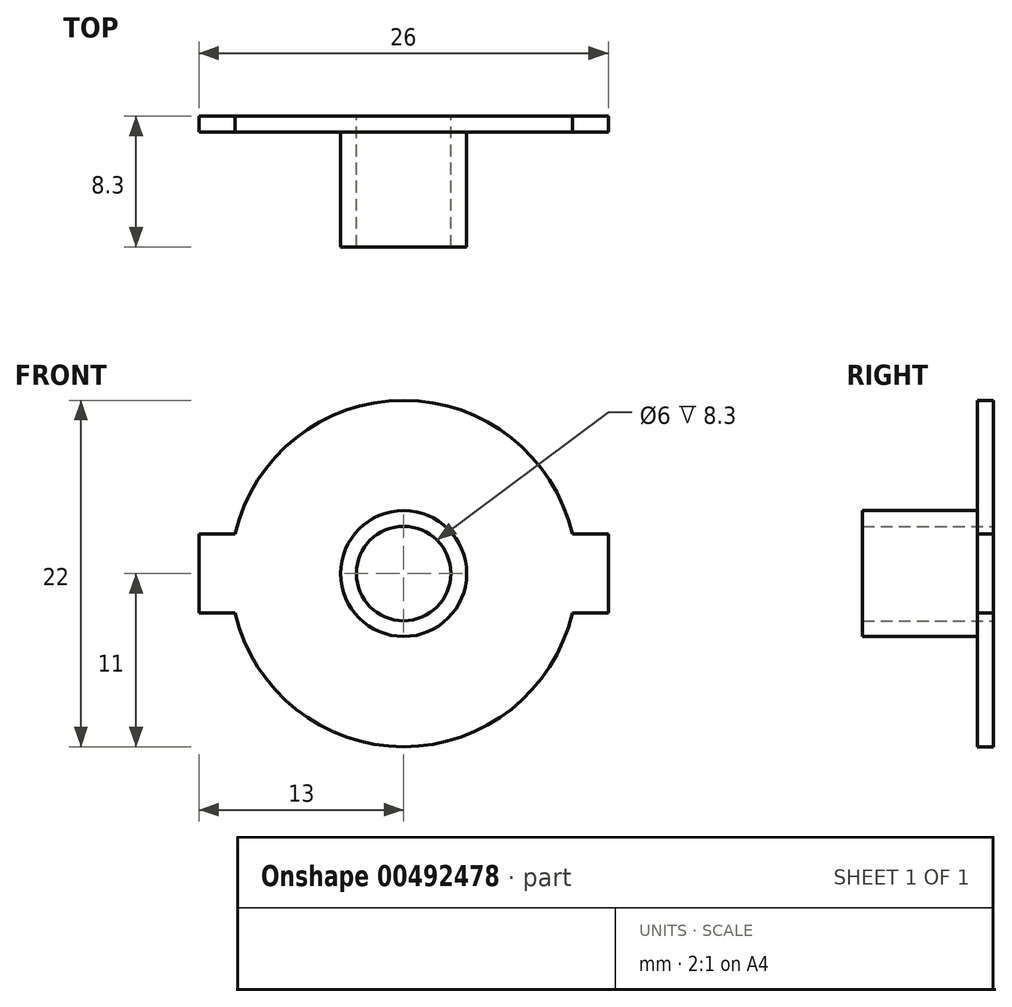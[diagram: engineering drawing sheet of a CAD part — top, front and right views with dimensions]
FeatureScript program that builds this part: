
annotation { "Feature Type Name" : "Feature", "Feature Type Description" : "" }
export const myFeature = defineFeature(function(context is Context, id is Id, definition is map)
    precondition{}
    {
        {
            var Q0;
            Q0=qCreatedBy(makeId("Front.planeOp"),FACE);
            var sketch = newSketch(context, id + "F0", { "sketchPlane" : qUnion([Q0])});
            skCircle(sketch, "E0", {"center": v(0, 0) * mm, "radius": 11 * mm});
            skSolve(sketch);
        }
        {
            var Q0;
            Q0=makeQuery(id+"F0.imprint","IMPRINT",FACE,{"disambiguationData":[TD([[makeQuery(id+"F0.imprint","IMPRINT",EDGE,{"derivedFrom":sQuery(id+"F0.wireOp",EDGE,"E0")}),1.0]])]});
            extrude(context, id + "F1", {"entities" : qUnion([Q0]), "depth" : 1 * mm});
        }
        {
            var Q0;
            Q0=makeQuery(id+"F1.opExtrude","CAP_FACE",FACE,{"disambiguationData":[OSD([sQuery(id+"F0.wireOp",EDGE,"E0")])],"isStart":false});
            var sketch = newSketch(context, id + "F2", { "sketchPlane" : qUnion([Q0])});
            skSolve(sketch);
        }
        {
            var Q0;
            Q0=makeQuery(id+"F1.opExtrude","CAP_FACE",FACE,{"disambiguationData":[OSD([sQuery(id+"F0.wireOp",EDGE,"E0")])],"isStart":true});
            var sketch = newSketch(context, id + "F3", { "sketchPlane" : qUnion([Q0])});
            skLineSegment(sketch, "E1.bottom", {"start": v(13, -2.5) * mm, "end": v(-13, -2.5) * mm});
            skLineSegment(sketch, "E1.top", {"start": v(13, 2.5) * mm, "end": v(-13, 2.5) * mm});
            skLineSegment(sketch, "E1.left", {"start": v(13, -2.5) * mm, "end": v(13, 2.5) * mm});
            skLineSegment(sketch, "E1.right", {"start": v(-13, -2.5) * mm, "end": v(-13, 2.5) * mm});
            skPoint(sketch, "E1.middle", {"position": v(0, 0) * mm});
            skSolve(sketch);
        }
        {
            var Q0;
            Q0=qSketchRegion(id+"F3",true);
            extrude(context, id + "F4", {"entities" : qUnion([Q0]), "operationType" : NewBodyOperationType.ADD, "oppositeDirection" : true, "depth" : 1 * mm});
        }
        {
            var Q0;
            Q0=makeQuery(id+"F2.imprint","IMPRINT",FACE,{"disambiguationData":[TD([[makeQuery(id+"F2.imprint","IMPRINT",EDGE,{"derivedFrom":makeQuery(id+"F1.opExtrude","CAP_EDGE",EDGE,{"disambiguationData":[OSD([sQuery(id+"F0.wireOp",EDGE,"E0")])],"isStart":false})}),1.0]])]});
            var sketch = newSketch(context, id + "F5", { "sketchPlane" : qUnion([Q0])});
            skCircle(sketch, "E2", {"center": v(0, 0) * mm, "radius": 3 * mm});
            skCircle(sketch, "E3.0", {"center": v(0, 0) * mm, "radius": 4 * mm});
            skSolve(sketch);
        }
        {
            var Q0;
            Q0=makeQuery(id+"F2.imprint","IMPRINT",FACE,{"disambiguationData":[TD([[makeQuery(id+"F2.imprint","IMPRINT",EDGE,{"derivedFrom":makeQuery(id+"F1.opExtrude","CAP_EDGE",EDGE,{"disambiguationData":[OSD([sQuery(id+"F0.wireOp",EDGE,"E0")])],"isStart":false})}),1.0]])]});
            var sketch = newSketch(context, id + "F6", { "sketchPlane" : qUnion([Q0])});
            skCircle(sketch, "E4", {"center": v(0, 0) * mm, "radius": 3 * mm});
            skSolve(sketch);
        }
        {
            var Q0;
            Q0=qSketchRegion(id+"F5",true);
            extrude(context, id + "F7", {"entities" : qUnion([Q0]), "operationType" : NewBodyOperationType.ADD, "depth" : 7.3 * mm});
        }
        {
            var Q0;
            Q0=qSketchRegion(id+"F6",true);
            extrude(context, id + "F8", {"entities" : qUnion([Q0]), "operationType" : NewBodyOperationType.REMOVE, "endBound" : BoundingType.THROUGH_ALL, "depth" : 25 * mm, "hasSecondDirection" : true, "secondDirectionBound" : SecondDirectionBoundingType.THROUGH_ALL, "secondDirectionOppositeDirection" : true, "secondDirectionDepth" : 25 * mm});
        }
    });
